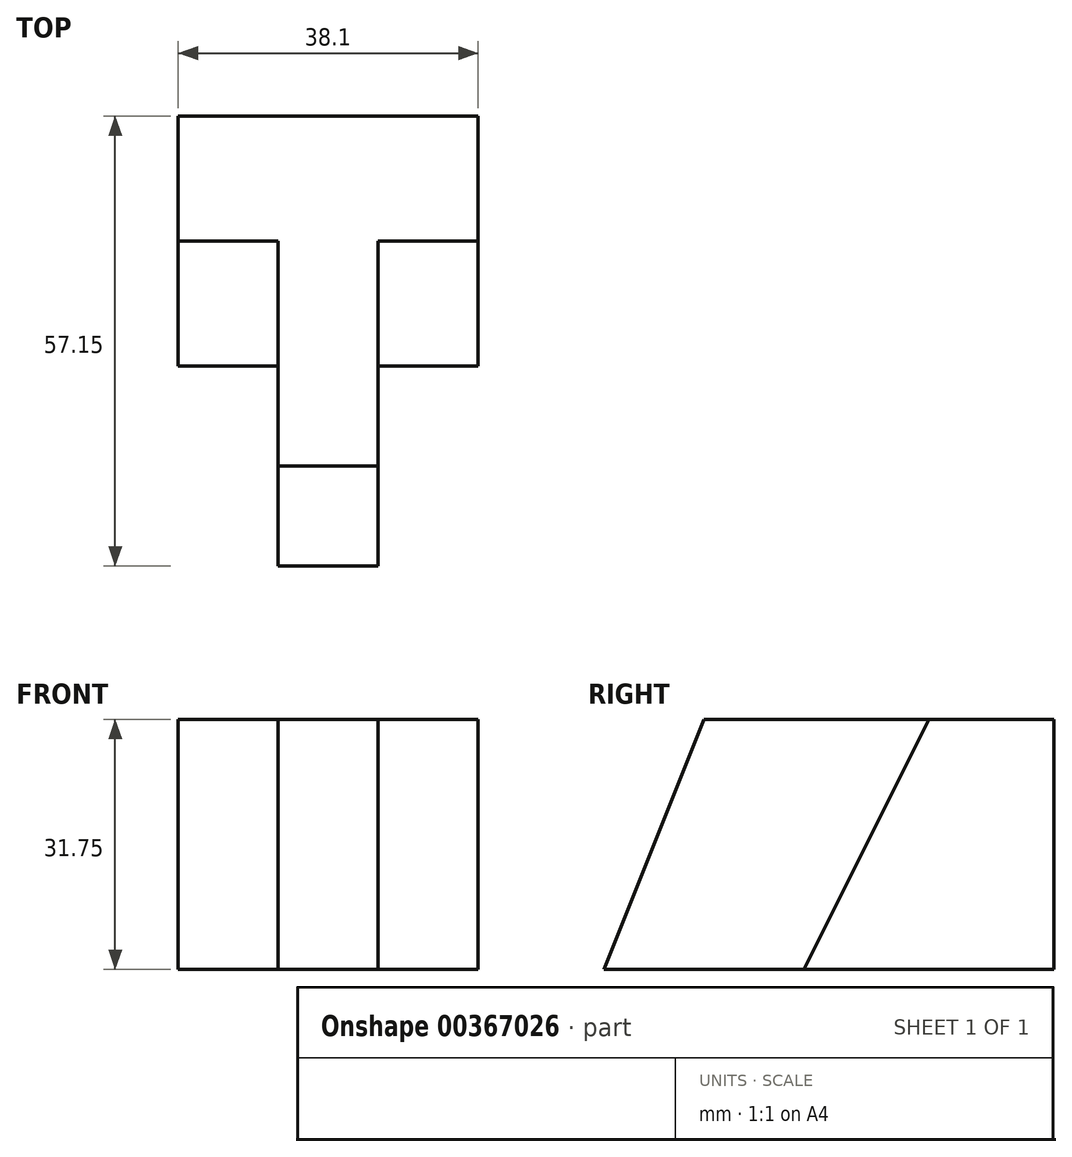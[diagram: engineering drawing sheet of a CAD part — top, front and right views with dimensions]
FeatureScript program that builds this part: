
annotation { "Feature Type Name" : "Feature", "Feature Type Description" : "" }
export const myFeature = defineFeature(function(context is Context, id is Id, definition is map)
    precondition{}
    {
        {
            var Q0;
            Q0=qCreatedBy(makeId("Top.planeOp"),FACE);
            var sketch = newSketch(context, id + "F0", { "sketchPlane" : qUnion([Q0])});
            skLineSegment(sketch, "E0", {"start": v(0, 0) * mm, "end": v(12.7, 0) * mm});
            skLineSegment(sketch, "E1", {"start": v(12.7, 0) * mm, "end": v(12.7, -25.4) * mm});
            skLineSegment(sketch, "E2", {"start": v(12.7, -25.4) * mm, "end": v(25.4, -25.4) * mm});
            skLineSegment(sketch, "E3", {"start": v(25.4, -25.4) * mm, "end": v(25.4, 0) * mm});
            skLineSegment(sketch, "E4", {"start": v(25.4, 0) * mm, "end": v(38.1, 0) * mm});
            skLineSegment(sketch, "E5", {"start": v(38.1, 0) * mm, "end": v(38.1, 31.75) * mm});
            skLineSegment(sketch, "E6", {"start": v(38.1, 31.75) * mm, "end": v(0, 31.75) * mm});
            skLineSegment(sketch, "E7", {"start": v(0, 31.75) * mm, "end": v(0, 0) * mm});
            skSolve(sketch);
        }
        {
            var Q0;
            Q0 = qSketchRegion(id + "F0", true);
            extrude(context, id + "F1", {"entities" : qUnion([Q0]), "depth" : 31.75 * mm});
        }
        {
            var Q0;
            Q0=makeQuery(id+"F1.opExtrude","SWEPT_FACE",FACE,{"disambiguationData":[OSD([sQuery(id+"F0.wireOp",EDGE,"E1")])]});
            var sketch = newSketch(context, id + "F2", { "sketchPlane" : qUnion([Q0])});
            skLineSegment(sketch, "E8", {"start": v(12.7, 31.75) * mm, "end": v(25.4, 0) * mm});
            skSolve(sketch);
        }
        {
            var Q0;
            {var subQ0=sQuery(id+"F2.wireOp",EDGE,"E8");Q0=makeQuery(id+"F2.imprint","IMPRINT",FACE,{"disambiguationData":[TD([[makeQuery(id+"F2.imprint","IMPRINT",EDGE,{"derivedFrom":subQ0}),1.0]])]});}
            extrude(context, id + "F3", {"entities" : qUnion([Q0]), "operationType" : NewBodyOperationType.REMOVE, "oppositeDirection" : true, "depth" : 25.4 * mm});
        }
        {
            var Q0;
            Q0=makeQuery(id+"F1.opExtrude","SWEPT_FACE",FACE,{"disambiguationData":[OSD([sQuery(id+"F0.wireOp",EDGE,"E7")])]});
            var sketch = newSketch(context, id + "F4", { "sketchPlane" : qUnion([Q0])});
            skLineSegment(sketch, "E9", {"start": v(-15.88, 31.75) * mm, "end": v(0, 0) * mm});
            skSolve(sketch);
        }
        {
            var Q0;
            Q0 = qSketchRegion(id + "F4", true);
            var Q1;
            {var subQ0=sQuery(id+"F4.wireOp",EDGE,"E9");Q1=makeQuery(id+"F4.imprint","IMPRINT",FACE,{"disambiguationData":[TD([[makeQuery(id+"F4.imprint","IMPRINT",EDGE,{"derivedFrom":subQ0}),1.0]])]});}
            extrude(context, id + "F5", {"entities" : qUnion([Q0, Q1]), "operationType" : NewBodyOperationType.REMOVE, "oppositeDirection" : true, "depth" : 12.7 * mm});
        }
        {
            var Q0;
            Q0=makeQuery(id+"F1.opExtrude","SWEPT_FACE",FACE,{"disambiguationData":[OSD([sQuery(id+"F0.wireOp",EDGE,"E5")])]});
            var sketch = newSketch(context, id + "F6", { "sketchPlane" : qUnion([Q0])});
            skLineSegment(sketch, "E10", {"start": v(15.88, 31.75) * mm, "end": v(0, 0) * mm});
            skSolve(sketch);
        }
        {
            var Q0;
            Q0 = qSketchRegion(id + "F6", true);
            var Q1;
            {var subQ0=sQuery(id+"F6.wireOp",EDGE,"E10");Q1=makeQuery(id+"F6.imprint","IMPRINT",FACE,{"disambiguationData":[TD([[makeQuery(id+"F6.imprint","IMPRINT",EDGE,{"derivedFrom":subQ0}),-1.0]])]});}
            extrude(context, id + "F7", {"entities" : qUnion([Q0, Q1]), "operationType" : NewBodyOperationType.REMOVE, "oppositeDirection" : true, "depth" : 12.7 * mm});
        }
    });
